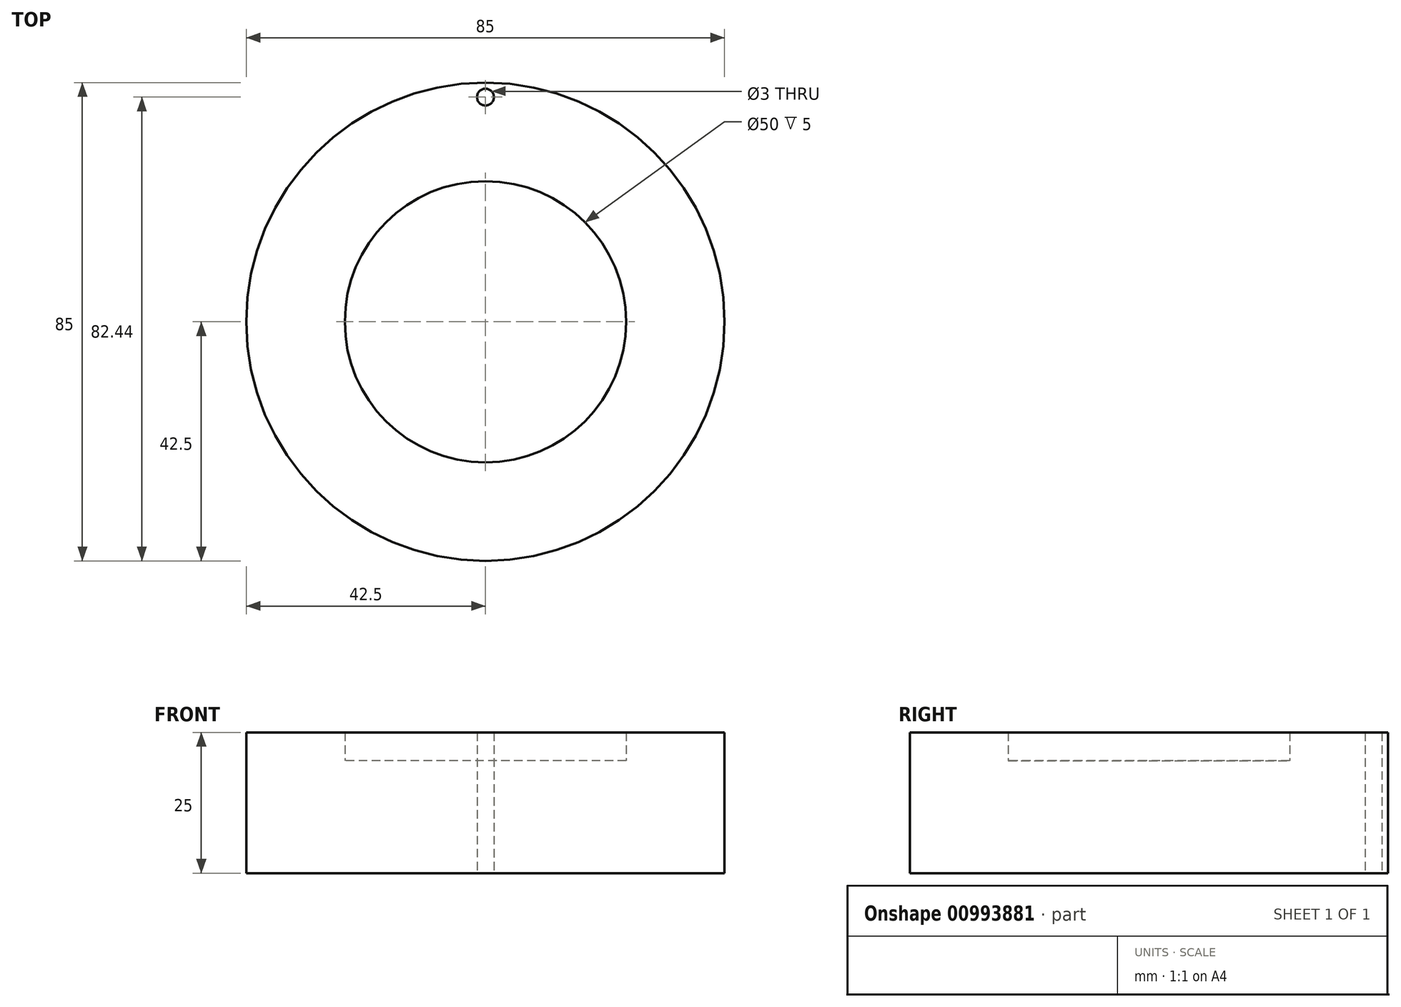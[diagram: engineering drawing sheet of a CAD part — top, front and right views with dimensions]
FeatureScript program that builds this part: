
annotation { "Feature Type Name" : "Feature", "Feature Type Description" : "" }
export const myFeature = defineFeature(function(context is Context, id is Id, definition is map)
    precondition{}
    {
        {
            var Q0;
            Q0=qCreatedBy(makeId("Top.planeOp"),FACE);
            var sketch = newSketch(context, id + "F0", { "sketchPlane" : qUnion([Q0])});
            skCircle(sketch, "E0", {"center": v(0, 0) * mm, "radius": 42.5 * mm});
            skCircle(sketch, "E1", {"center": v(0, 0) * mm, "radius": 25 * mm});
            skCircle(sketch, "E2", {"center": v(0, 39.94) * mm, "radius": 1.5 * mm});
            skSolve(sketch);
        }
        {
            var Q0;
            Q0 = qSketchRegion(id + "F0", true);
            var Q1;
            Q1=makeQuery(id+"F0.imprint","IMPRINT",FACE,{"disambiguationData":[TD([[makeQuery(id+"F0.imprint","IMPRINT",EDGE,{"derivedFrom":sQuery(id+"F0.wireOp",EDGE,"E1")}),1.0]])]});
            extrude(context, id + "F1", {"entities" : qUnion([Q0, Q1]), "depth" : 5 * mm, "offsetDistance" : 25 * mm});
        }
        {
            var Q0;
            Q0=makeQuery(id+"F0.imprint","IMPRINT",FACE,{"disambiguationData":[TD([[makeQuery(id+"F0.imprint","IMPRINT",EDGE,{"derivedFrom":sQuery(id+"F0.wireOp",EDGE,"E1")}),1.0]])]});
            extrude(context, id + "F2", {"entities" : qUnion([Q0]), "operationType" : NewBodyOperationType.ADD, "depth" : 20 * mm, "offsetDistance" : 25 * mm});
        }
        {
            var Q0;
            Q0 = qSketchRegion(id + "F0", true);
            extrude(context, id + "F3", {"entities" : qUnion([Q0]), "operationType" : NewBodyOperationType.ADD, "depth" : 25 * mm, "offsetDistance" : 25 * mm});
        }
    });
